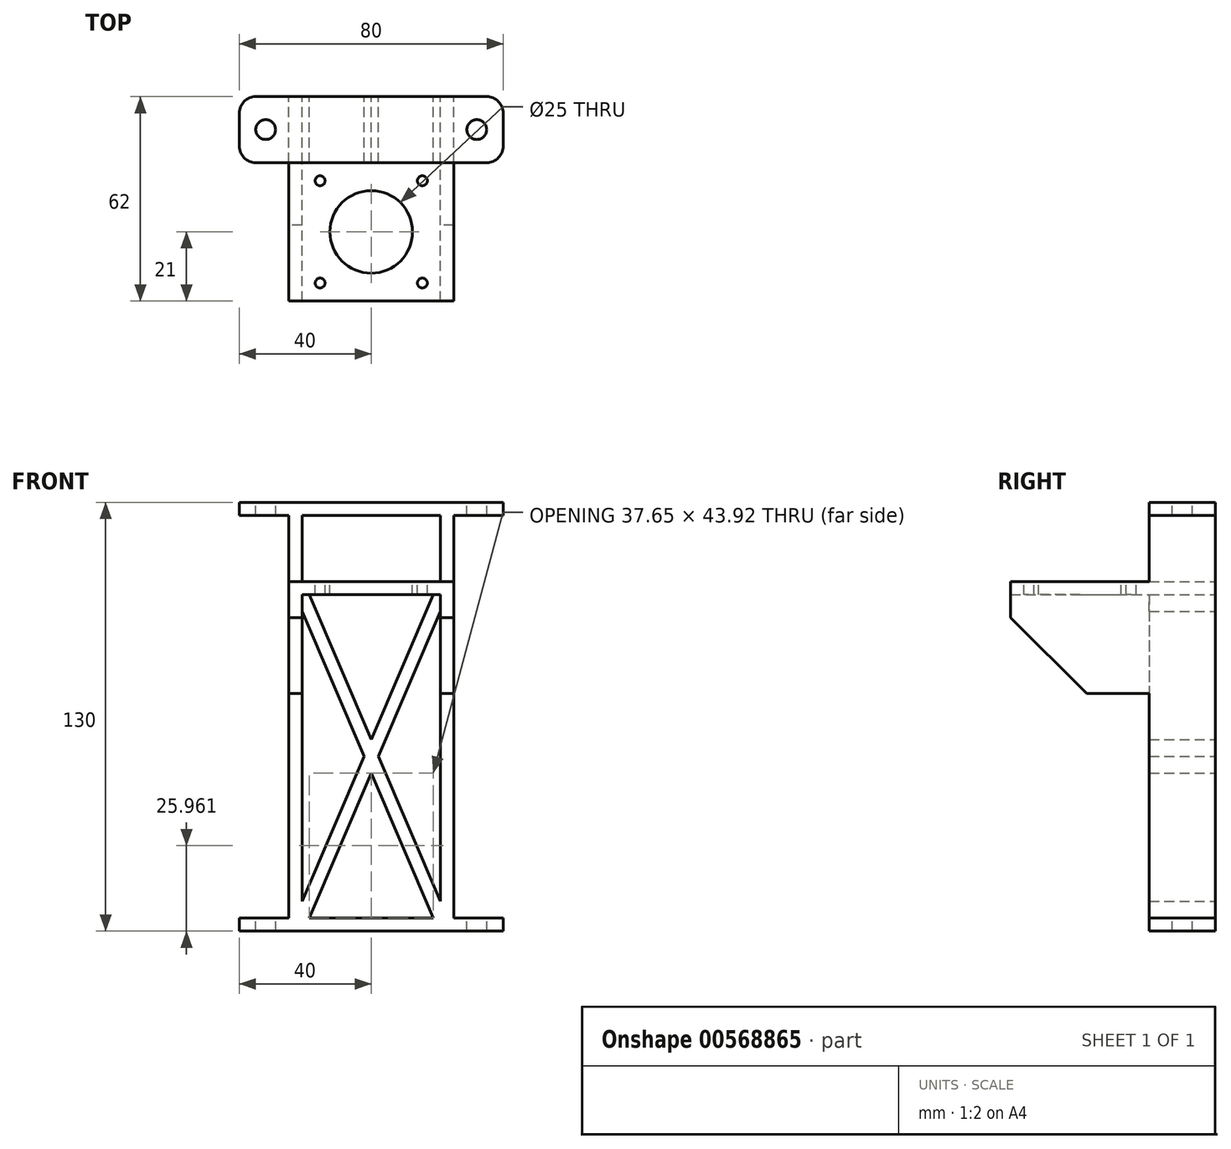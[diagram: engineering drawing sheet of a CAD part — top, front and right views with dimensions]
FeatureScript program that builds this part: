
annotation { "Feature Type Name" : "Feature", "Feature Type Description" : "" }
export const myFeature = defineFeature(function(context is Context, id is Id, definition is map)
    precondition{}
    {
        {
            var Q0;
            Q0=qCreatedBy(makeId("Front.planeOp"),FACE);
            var sketch = newSketch(context, id + "F0", { "sketchPlane" : qUnion([Q0])});
            skLineSegment(sketch, "E0", {"start": v(0, 211.78) * mm, "end": v(0, -24.75) * mm, "construction": true});
            skLineSegment(sketch, "E1", {"start": v(0, 130) * mm, "end": v(-40, 130) * mm});
            skLineSegment(sketch, "E2", {"start": v(-40, 130) * mm, "end": v(-40, 126) * mm});
            skLineSegment(sketch, "E3", {"start": v(-40, 126) * mm, "end": v(-25, 126) * mm});
            skLineSegment(sketch, "E4", {"start": v(-25, 126) * mm, "end": v(-25, 4) * mm});
            skLineSegment(sketch, "E5", {"start": v(-25, 4) * mm, "end": v(-40, 4) * mm});
            skLineSegment(sketch, "E6", {"start": v(-40, 4) * mm, "end": v(-40, 0) * mm});
            skLineSegment(sketch, "E7", {"start": v(-40, 0) * mm, "end": v(0, 0) * mm});
            skLineSegment(sketch, "E8", {"start": v(0, 126) * mm, "end": v(-21, 126) * mm});
            skLineSegment(sketch, "E9", {"start": v(-21, 126) * mm, "end": v(-21, 106) * mm});
            skLineSegment(sketch, "E10", {"start": v(-21, 106) * mm, "end": v(0, 106) * mm});
            skLineSegment(sketch, "E11", {"start": v(0, 102) * mm, "end": v(-21, 102) * mm});
            skLineSegment(sketch, "E12", {"start": v(-21, 102) * mm, "end": v(-21, 4) * mm});
            skLineSegment(sketch, "E13", {"start": v(-21, 4) * mm, "end": v(0, 4) * mm});
            skLineSegment(sketch, "E14", {"start": v(-21, 106) * mm, "end": v(-25, 106) * mm});
            skLineSegment(sketch, "E15", {"start": v(-25, 72) * mm, "end": v(-21, 72) * mm});
            skLineSegment(sketch, "E16.MirrorCS", {"start": v(0, 126) * mm, "end": v(21, 126) * mm});
            skLineSegment(sketch, "E17.MirrorCS", {"start": v(0, 130) * mm, "end": v(40, 130) * mm});
            skLineSegment(sketch, "E18.MirrorCS", {"start": v(40, 130) * mm, "end": v(40, 126) * mm});
            skLineSegment(sketch, "E19.MirrorCS", {"start": v(40, 126) * mm, "end": v(25, 126) * mm});
            skLineSegment(sketch, "E20.MirrorCS", {"start": v(25, 126) * mm, "end": v(25, 4) * mm});
            skLineSegment(sketch, "E21.MirrorCS", {"start": v(21, 126) * mm, "end": v(21, 106) * mm});
            skLineSegment(sketch, "E22.MirrorCS", {"start": v(21, 106) * mm, "end": v(0, 106) * mm});
            skLineSegment(sketch, "E23.MirrorCS", {"start": v(21, 106) * mm, "end": v(25, 106) * mm});
            skLineSegment(sketch, "E24.MirrorCS", {"start": v(21, 102) * mm, "end": v(21, 4) * mm});
            skLineSegment(sketch, "E25.MirrorCS", {"start": v(0, 102) * mm, "end": v(21, 102) * mm});
            skLineSegment(sketch, "E26.MirrorCS", {"start": v(21, 4) * mm, "end": v(0, 4) * mm});
            skLineSegment(sketch, "E27.MirrorCS", {"start": v(40, 0) * mm, "end": v(0, 0) * mm});
            skLineSegment(sketch, "E28.MirrorCS", {"start": v(40, 4) * mm, "end": v(40, 0) * mm});
            skLineSegment(sketch, "E29.MirrorCS", {"start": v(25, 4) * mm, "end": v(40, 4) * mm});
            skLineSegment(sketch, "E30.MirrorCS", {"start": v(25, 72) * mm, "end": v(21, 72) * mm});
            skLineSegment(sketch, "E31", {"start": v(-21, 4) * mm, "end": v(0, 53) * mm, "construction": true});
            skLineSegment(sketch, "E32", {"start": v(-21, 102) * mm, "end": v(0, 53) * mm, "construction": true});
            skLineSegment(sketch, "E33", {"start": v(0, 53) * mm, "end": v(21, 102) * mm, "construction": true});
            skLineSegment(sketch, "E34", {"start": v(0, 53) * mm, "end": v(21, 4) * mm, "construction": true});
            skLineSegment(sketch, "E35.0", {"start": v(-21, 96.92) * mm, "end": v(-2.18, 53) * mm});
            skLineSegment(sketch, "E35.1", {"start": v(-21, 9.08) * mm, "end": v(-2.18, 53) * mm});
            skLineSegment(sketch, "E36.0", {"start": v(-18.82, 4) * mm, "end": v(0, 47.92) * mm});
            skLineSegment(sketch, "E37.0", {"start": v(-18.82, 102) * mm, "end": v(0, 58.08) * mm});
            skLineSegment(sketch, "E38.MirrorCS", {"start": v(18.82, 102) * mm, "end": v(0, 58.08) * mm});
            skLineSegment(sketch, "E39.MirrorCS", {"start": v(21, 96.92) * mm, "end": v(2.18, 53) * mm});
            skLineSegment(sketch, "E40.MirrorCS", {"start": v(21, 9.08) * mm, "end": v(2.18, 53) * mm});
            skLineSegment(sketch, "E41.MirrorCS", {"start": v(18.82, 4) * mm, "end": v(0, 47.92) * mm});
            skSolve(sketch);
        }
        {
            var Q0;
            Q0 = qSketchRegion(id + "F0", true);
            var Q1;
            {var subQ1=sQuery(id+"F0.wireOp",EDGE,"E35.0");Q1=makeQuery(id+"F0.imprint","IMPRINT",FACE,{"disambiguationData":[TD([[makeQuery(id+"F0.imprint","IMPRINT",EDGE,{"derivedFrom":subQ1}),1.0]])]});}
            extrude(context, id + "F1", {"entities" : qUnion([Q0, Q1]), "depth" : 20 * mm, "offsetDistance" : 25 * mm});
        }
        {
            var Q0;
            Q0=makeQuery(id+"F0.imprint","IMPRINT",FACE,{"disambiguationData":[TD([[makeQuery(id+"F0.imprint","IMPRINT",EDGE,{"derivedFrom":sQuery(id+"F0.wireOp",EDGE,"E10")}),-1.0]])]});
            extrude(context, id + "F2", {"entities" : qUnion([Q0]), "operationType" : NewBodyOperationType.ADD, "depth" : 62 * mm, "offsetDistance" : 25 * mm});
        }
        {
            var Q0;
            Q0=makeQuery(id+"F1.opExtrude","SWEPT_FACE",FACE,{"disambiguationData":[OSD([sQuery(id+"F0.wireOp",EDGE,"E1"),sQuery(id+"F0.wireOp",EDGE,"E17.MirrorCS")])]});
            var sketch = newSketch(context, id + "F3", { "sketchPlane" : qUnion([Q0])});
            skLineSegment(sketch, "E42.0", {"start": v(-40, -20) * mm, "end": v(40, -20) * mm, "construction": true});
            skLineSegment(sketch, "E42.1", {"start": v(40, -20) * mm, "end": v(40, 0) * mm, "construction": true});
            skLineSegment(sketch, "E42.2", {"start": v(-40, 0) * mm, "end": v(40, 0) * mm, "construction": true});
            skLineSegment(sketch, "E42.3", {"start": v(-40, -20) * mm, "end": v(-40, 0) * mm, "construction": true});
            skLineSegment(sketch, "E43.0", {"start": v(21, -62) * mm, "end": v(21, -20) * mm, "construction": true});
            skLineSegment(sketch, "E43.1", {"start": v(-21, -62) * mm, "end": v(-21, -20) * mm, "construction": true});
            skLineSegment(sketch, "E44", {"start": v(-21, -62) * mm, "end": v(21, -62) * mm, "construction": true});
            skLineSegment(sketch, "E45", {"start": v(-21, -62) * mm, "end": v(21, -20) * mm, "construction": true});
            skLineSegment(sketch, "E46", {"start": v(-21, -20) * mm, "end": v(21, -62) * mm, "construction": true});
            skCircle(sketch, "E47", {"center": v(0, -41) * mm, "radius": 12.5 * mm});
            skCircle(sketch, "E48", {"center": v(-15.5, -56.5) * mm, "radius": 1.5 * mm});
            skCircle(sketch, "E49", {"center": v(15.5, -56.5) * mm, "radius": 1.5 * mm});
            skCircle(sketch, "E50", {"center": v(15.5, -25.5) * mm, "radius": 1.5 * mm});
            skCircle(sketch, "E51", {"center": v(-15.5, -25.5) * mm, "radius": 1.5 * mm});
            skCircle(sketch, "E52", {"center": v(-32, -10) * mm, "radius": 3 * mm});
            skCircle(sketch, "E53", {"center": v(32, -10) * mm, "radius": 3 * mm});
            skLineSegment(sketch, "E54", {"start": v(-40, -10) * mm, "end": v(40, -10) * mm, "construction": true});
            skSolve(sketch);
        }
        {
            var Q0;
            Q0 = qSketchRegion(id + "F3", true);
            extrude(context, id + "F4", {"entities" : qUnion([Q0]), "operationType" : NewBodyOperationType.REMOVE, "oppositeDirection" : true, "depth" : 130 * mm, "offsetDistance" : 25 * mm});
        }
        {
            var Q0;
            Q0=makeQuery(id+"F2.opExtrude","CAP_EDGE",EDGE,{"disambiguationData":[OSD([sQuery(id+"F0.wireOp",EDGE,"E15")])],"isStart":false});
            var Q1;
            Q1=makeQuery(id+"F2.opExtrude","CAP_EDGE",EDGE,{"disambiguationData":[OSD([sQuery(id+"F0.wireOp",EDGE,"E30.MirrorCS")])],"isStart":false});
            chamfer(context, id + "F5", {"entities" : qUnion([Q0, Q1]), "width" : 23 * mm, "tangentPropagation" : true});
        }
        {
            var Q0;
            Q0=makeQuery(id+"F1.opExtrude","CAP_EDGE",EDGE,{"disambiguationData":[OSD([sQuery(id+"F0.wireOp",EDGE,"E2")])],"isStart":true});
            var Q1;
            Q1=makeQuery(id+"F1.opExtrude","CAP_EDGE",EDGE,{"disambiguationData":[OSD([sQuery(id+"F0.wireOp",EDGE,"E2")])],"isStart":false});
            var Q2;
            Q2=makeQuery(id+"F1.opExtrude","CAP_EDGE",EDGE,{"disambiguationData":[OSD([sQuery(id+"F0.wireOp",EDGE,"E18.MirrorCS")])],"isStart":true});
            var Q3;
            Q3=makeQuery(id+"F1.opExtrude","CAP_EDGE",EDGE,{"disambiguationData":[OSD([sQuery(id+"F0.wireOp",EDGE,"E18.MirrorCS")])],"isStart":false});
            var Q4;
            Q4=makeQuery(id+"F1.opExtrude","CAP_EDGE",EDGE,{"disambiguationData":[OSD([sQuery(id+"F0.wireOp",EDGE,"E28.MirrorCS")])],"isStart":true});
            var Q5;
            Q5=makeQuery(id+"F1.opExtrude","CAP_EDGE",EDGE,{"disambiguationData":[OSD([sQuery(id+"F0.wireOp",EDGE,"E28.MirrorCS")])],"isStart":false});
            var Q6;
            Q6=makeQuery(id+"F1.opExtrude","CAP_EDGE",EDGE,{"disambiguationData":[OSD([sQuery(id+"F0.wireOp",EDGE,"E6")])],"isStart":true});
            var Q7;
            Q7=makeQuery(id+"F1.opExtrude","CAP_EDGE",EDGE,{"disambiguationData":[OSD([sQuery(id+"F0.wireOp",EDGE,"E6")])],"isStart":false});
            fillet(context, id + "F6", {"entities" : qUnion([Q0, Q1, Q2, Q3, Q4, Q5, Q6, Q7]), "radius" : 5 * mm, "tangentPropagation" : true, "allowEdgeOverflow" : false});
        }
    });
